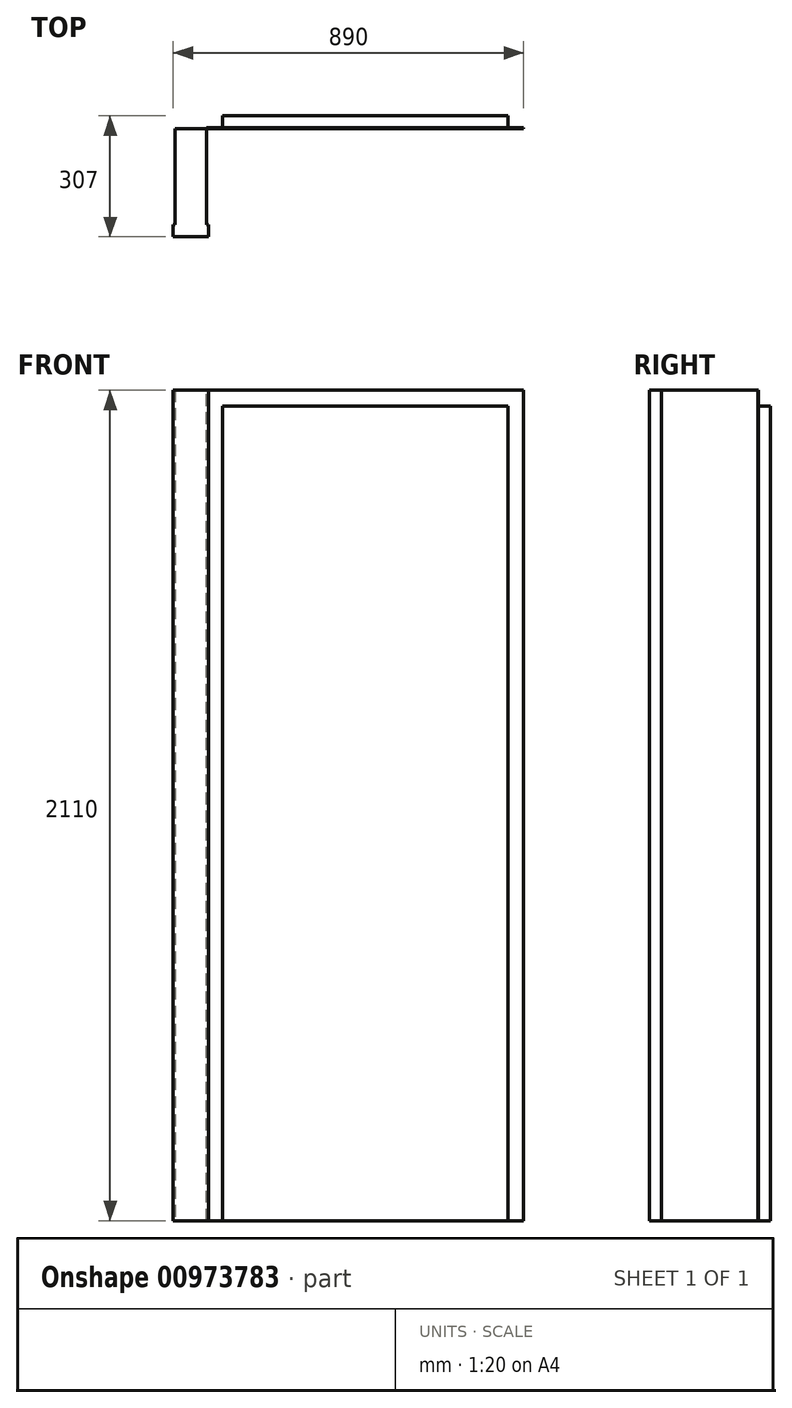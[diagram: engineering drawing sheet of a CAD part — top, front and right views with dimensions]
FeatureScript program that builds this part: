
annotation { "Feature Type Name" : "Feature", "Feature Type Description" : "" }
export const myFeature = defineFeature(function(context is Context, id is Id, definition is map)
    precondition{}
    {
        {
            var Q0;
            Q0=qCreatedBy(makeId("Front.planeOp"),FACE);
            var sketch = newSketch(context, id + "F0", { "sketchPlane" : qUnion([Q0])});
            skLineSegment(sketch, "E0.bottom", {"start": v(0, 0) * mm, "end": v(-725, 0) * mm});
            skLineSegment(sketch, "E0.top", {"start": v(0, 2070) * mm, "end": v(-725, 2070) * mm});
            skLineSegment(sketch, "E0.left", {"start": v(0, 0) * mm, "end": v(0, 2070) * mm});
            skLineSegment(sketch, "E0.right", {"start": v(-725, 0) * mm, "end": v(-725, 2070) * mm});
            skSolve(sketch);
        }
        {
            var Q0;
            Q0 = qSketchRegion(id + "F0", true);
            extrude(context, id + "F1", {"entities" : qUnion([Q0]), "depth" : 30 * mm, "offsetDistance" : 25 * mm});
        }
        {
            var Q0;
            Q0=makeQuery(id+"F1.opExtrude","CAP_FACE",FACE,{"disambiguationData":[OSD([sQuery(id+"F0.wireOp",EDGE,"E0.bottom"),sQuery(id+"F0.wireOp",EDGE,"E0.top"),sQuery(id+"F0.wireOp",EDGE,"E0.left"),sQuery(id+"F0.wireOp",EDGE,"E0.right")])],"isStart":false});
            var sketch = newSketch(context, id + "F2", { "sketchPlane" : qUnion([Q0])});
            skLineSegment(sketch, "E1.bottom", {"start": v(-725, 0) * mm, "end": v(-765, 0) * mm});
            skLineSegment(sketch, "E1.top", {"start": v(-725, 2110) * mm, "end": v(-765, 2110) * mm});
            skLineSegment(sketch, "E1.left", {"start": v(-725, 0) * mm, "end": v(-725, 2070) * mm});
            skLineSegment(sketch, "E1.right", {"start": v(-765, 0) * mm, "end": v(-765, 2110) * mm});
            skLineSegment(sketch, "E2.bottom", {"start": v(-725, 2110) * mm, "end": v(0, 2110) * mm});
            skLineSegment(sketch, "E2.top", {"start": v(-725, 2070) * mm, "end": v(0, 2070) * mm});
            skLineSegment(sketch, "E3.bottom", {"start": v(0, 2110) * mm, "end": v(40, 2110) * mm});
            skLineSegment(sketch, "E3.top", {"start": v(0, 0) * mm, "end": v(40, 0) * mm});
            skLineSegment(sketch, "E3.left", {"start": v(0, 2070) * mm, "end": v(0, 0) * mm});
            skLineSegment(sketch, "E3.right", {"start": v(40, 2110) * mm, "end": v(40, 0) * mm});
            skSolve(sketch);
        }
        {
            var Q0;
            Q0 = qSketchRegion(id + "F2", true);
            extrude(context, id + "F3", {"entities" : qUnion([Q0]), "depth" : 2 * mm, "offsetDistance" : 25 * mm});
        }
        {
            var Q0;
            Q0=makeQuery(id+"F3.opExtrude","CAP_FACE",FACE,{"disambiguationData":[OSD([sQuery(id+"F2.wireOp",EDGE,"E1.bottom"),sQuery(id+"F2.wireOp",EDGE,"E1.top"),sQuery(id+"F2.wireOp",EDGE,"E1.left"),sQuery(id+"F2.wireOp",EDGE,"E1.right"),sQuery(id+"F2.wireOp",EDGE,"E2.bottom"),sQuery(id+"F2.wireOp",EDGE,"E2.top"),sQuery(id+"F2.wireOp",EDGE,"E3.bottom"),sQuery(id+"F2.wireOp",EDGE,"E3.top"),sQuery(id+"F2.wireOp",EDGE,"E3.left"),sQuery(id+"F2.wireOp",EDGE,"E3.right")])],"isStart":false});
            var sketch = newSketch(context, id + "F4", { "sketchPlane" : qUnion([Q0])});
            skLineSegment(sketch, "E4.bottom", {"start": v(-765, 2110) * mm, "end": v(-845, 2110) * mm});
            skLineSegment(sketch, "E4.top", {"start": v(-765, 0) * mm, "end": v(-845, 0) * mm});
            skLineSegment(sketch, "E4.left", {"start": v(-765, 2110) * mm, "end": v(-765, 0) * mm});
            skLineSegment(sketch, "E4.right", {"start": v(-845, 2110) * mm, "end": v(-845, 0) * mm});
            skSolve(sketch);
        }
        {
            var Q0;
            Q0 = qSketchRegion(id + "F4", true);
            extrude(context, id + "F5", {"entities" : qUnion([Q0]), "depth" : 245 * mm, "offsetDistance" : 25 * mm});
        }
        {
            var Q0;
            Q0=makeQuery(id+"F5.opExtrude","SWEPT_FACE",FACE,{"disambiguationData":[OSD([sQuery(id+"F4.wireOp",EDGE,"E4.bottom")])]});
            var sketch = newSketch(context, id + "F6", { "sketchPlane" : qUnion([Q0])});
            skLineSegment(sketch, "E5.bottom", {"start": v(-850, -277) * mm, "end": v(-760, -277) * mm});
            skLineSegment(sketch, "E5.top", {"start": v(-850, -307) * mm, "end": v(-760, -307) * mm});
            skLineSegment(sketch, "E5.left", {"start": v(-850, -277) * mm, "end": v(-850, -307) * mm});
            skLineSegment(sketch, "E5.right", {"start": v(-760, -277) * mm, "end": v(-760, -307) * mm});
            skSolve(sketch);
        }
        {
            var Q0;
            Q0 = qSketchRegion(id + "F6", true);
            extrude(context, id + "F7", {"entities" : qUnion([Q0]), "operationType" : NewBodyOperationType.ADD, "oppositeDirection" : true, "depth" : 2110 * mm, "offsetDistance" : 25 * mm});
        }
    });
